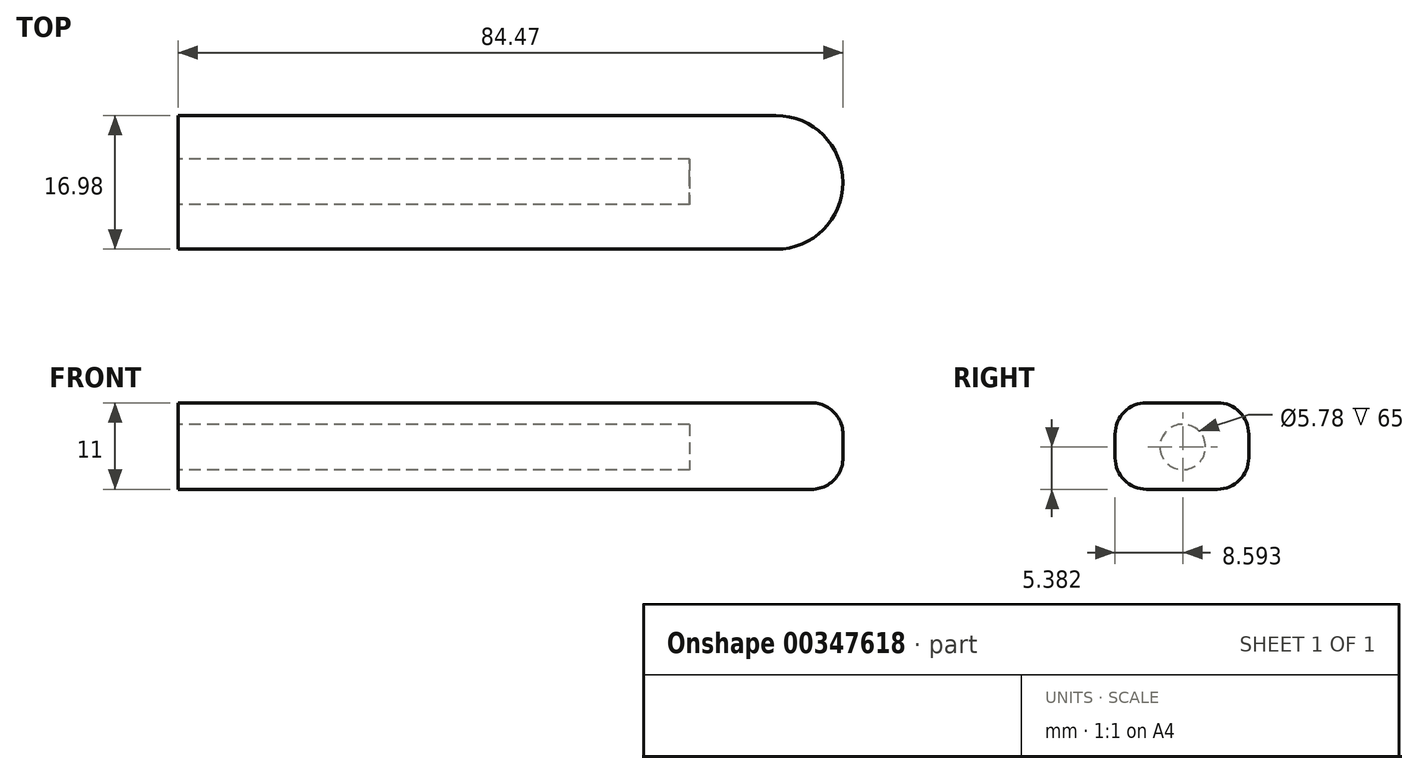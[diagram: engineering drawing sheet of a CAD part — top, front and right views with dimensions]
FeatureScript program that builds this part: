
annotation { "Feature Type Name" : "Feature", "Feature Type Description" : "" }
export const myFeature = defineFeature(function(context is Context, id is Id, definition is map)
    precondition{}
    {
        {
            var Q0;
            Q0=qCreatedBy(makeId("Top.planeOp"),FACE);
            var sketch = newSketch(context, id + "F0", { "sketchPlane" : qUnion([Q0])});
            skLineSegment(sketch, "E0.bottom", {"start": v(-40, 11.22) * mm, "end": v(35.98, 11.22) * mm});
            skLineSegment(sketch, "E0.top", {"start": v(-40, -5.76) * mm, "end": v(35.98, -5.76) * mm});
            skLineSegment(sketch, "E0.left", {"start": v(-40, 11.22) * mm, "end": v(-40, -5.76) * mm});
            skArc(sketch, "E1", {"start": v(35.98, -5.76) * mm, "mid": v(44.47, 2.73) * mm, "end": v(35.98, 11.22) * mm});
            skSolve(sketch);
        }
        {
            var Q0;
            Q0 = qSketchRegion(id + "F0", true);
            extrude(context, id + "F1", {"entities" : qUnion([Q0]), "depth" : 11 * mm});
        }
        {
            var Q0;
            Q0=makeQuery(id+"F1.opExtrude","CAP_EDGE",EDGE,{"disambiguationData":[OSD([sQuery(id+"F0.wireOp",EDGE,"E0.top")])],"isStart":false});
            var Q1;
            Q1=makeQuery(id+"F1.opExtrude","CAP_EDGE",EDGE,{"disambiguationData":[OSD([sQuery(id+"F0.wireOp",EDGE,"E1")])],"isStart":false});
            var Q2;
            Q2=makeQuery(id+"F1.opExtrude","CAP_EDGE",EDGE,{"disambiguationData":[OSD([sQuery(id+"F0.wireOp",EDGE,"E0.bottom")])],"isStart":false});
            fillet(context, id + "F2", {"entities" : qUnion([Q0, Q1, Q2]), "radius" : 4 * mm, "tangentPropagation" : true, "allowEdgeOverflow" : false});
        }
        {
            var Q0;
            Q0=makeQuery(id+"F1.opExtrude","CAP_EDGE",EDGE,{"disambiguationData":[OSD([sQuery(id+"F0.wireOp",EDGE,"E0.bottom")])],"isStart":true});
            var Q1;
            Q1=makeQuery(id+"F1.opExtrude","CAP_EDGE",EDGE,{"disambiguationData":[OSD([sQuery(id+"F0.wireOp",EDGE,"E0.top")])],"isStart":true});
            var Q2;
            Q2=makeQuery(id+"F1.opExtrude","CAP_EDGE",EDGE,{"disambiguationData":[OSD([sQuery(id+"F0.wireOp",EDGE,"E1")])],"isStart":true});
            fillet(context, id + "F3", {"entities" : qUnion([Q0, Q1, Q2]), "radius" : 4 * mm, "tangentPropagation" : true, "allowEdgeOverflow" : false});
        }
        {
            var Q0;
            Q0=makeQuery(id+"F1.opExtrude","SWEPT_FACE",FACE,{"disambiguationData":[OSD([sQuery(id+"F0.wireOp",EDGE,"E0.left")])]});
            var sketch = newSketch(context, id + "F4", { "sketchPlane" : qUnion([Q0])});
            skCircle(sketch, "E2", {"center": v(-2.83, 5.38) * mm, "radius": 2.89 * mm});
            skSolve(sketch);
        }
        {
            var Q0;
            Q0 = qSketchRegion(id + "F4", true);
            extrude(context, id + "F5", {"entities" : qUnion([Q0]), "operationType" : NewBodyOperationType.REMOVE, "oppositeDirection" : true, "depth" : 65 * mm});
        }
    });
